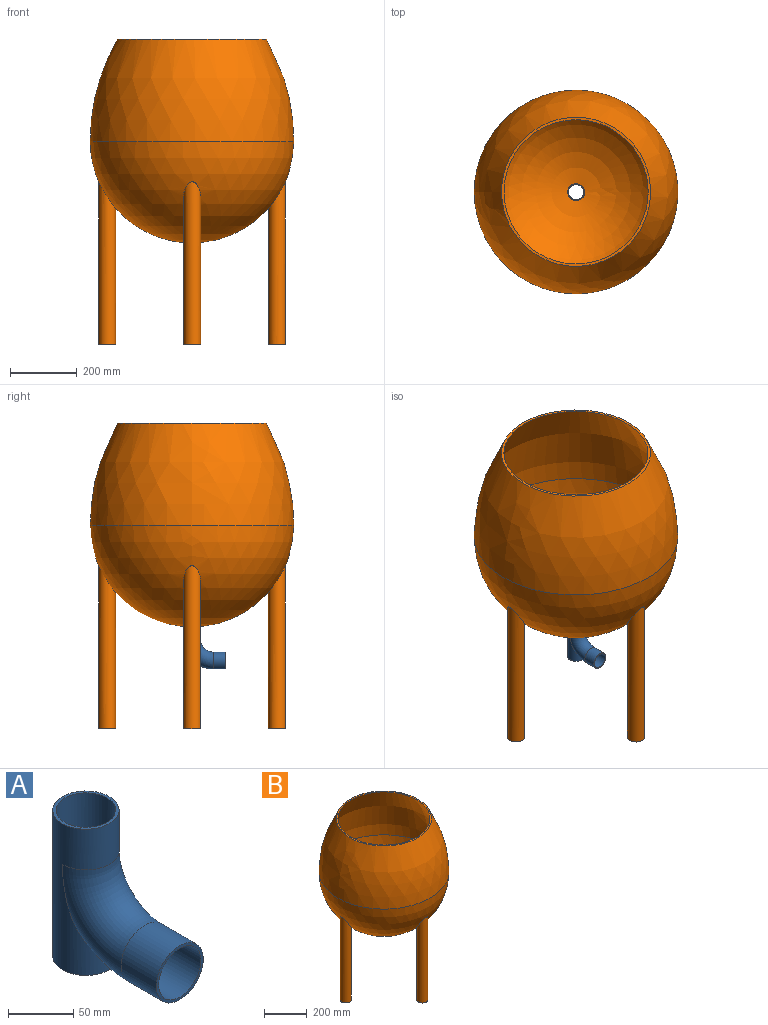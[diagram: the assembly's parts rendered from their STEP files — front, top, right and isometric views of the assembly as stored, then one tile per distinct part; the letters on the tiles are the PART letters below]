
ASSEMBLY  parts=2 mates=1
PART A: 9 faces, bbox 50.8x134.3x137 mm
  f0: torus R=63.5mm, axis (-1,0,0), area 10133.9mm2, adj f1,f3
  f1: cylinder r=25.4mm len=50.8mm, axis (0,1,0), area 6080.5mm2, adj f0,f2
  f2: plane 50.8x50.8mm, normal (0,-1,0), area 385.1mm2, adj f1,f7
  f3: cylinder r=25.4mm len=137mm, axis (0,0,-1), area 16975mm2, adj f0,f4,f5
  f4: plane 50.8x50.8mm, normal (0,0,1), area 385.1mm2, adj f3,f8
  f5: plane 50.8x50.8mm, normal (0,0,-1), area 385.1mm2, adj f3,f8
  f6: torus R=63.5mm, axis (-1,0,0), area 9453.9mm2, adj f7,f8
  f7: cylinder r=22.86mm len=45.72mm, axis (0,1,0), area 5472.4mm2, adj f2,f6
  f8: cylinder r=22.86mm len=137mm, axis (0,0,-1), area 15502.7mm2, adj f4,f5,f6
PART B: 14 faces, bbox 609.6x609.6x914.4 mm
  f0: revolved ~609.6x609.6mm, area 556176.5mm2, adj f1,f2
  f1: sphere r=304.8mm, area 566511.4mm2, adj f0,f5,f7,f9,f11,f13
  f2: plane 446.26x446.26mm, normal (0,0,1), area 10128.3mm2, adj f0,f3
  f3: revolved ~596.9x596.9mm, area 543349.5mm2, adj f2,f4
  f4: sphere r=298.45mm, area 557627.9mm2, adj f3,f5
  f5: cylinder r=25.4mm len=50.8mm, axis (0,0,1), area 1017mm2, adj f1,f4
  f6: plane 50.8x50.8mm, normal (0,0,-1), area 2026.8mm2, adj f7
  f7: cylinder r=25.4mm len=487.79mm, axis (0,0,-1), area 71088.8mm2, adj f1,f6
  f8: plane 50.8x50.8mm, normal (0,0,-1), area 2026.8mm2, adj f9
  f9: cylinder r=25.4mm len=487.79mm, axis (0,0,-1), area 71089.1mm2, adj f1,f8
  f10: plane 50.8x50.8mm, normal (0,0,-1), area 2026.8mm2, adj f11
  f11: cylinder r=25.4mm len=487.79mm, axis (0,0,-1), area 71089.5mm2, adj f1,f10
  f12: plane 50.8x50.8mm, normal (0,0,-1), area 2026.8mm2, adj f13
  f13: cylinder r=25.4mm len=487.79mm, axis (0,0,-1), area 71086.4mm2, adj f1,f12
PLACE A t=(0,-63.5,-405.34)mm
PLACE B at identity
MATE fastened A.f3 <-> B.f5  axis (0,0,1) through (0,0,-303.74)mm
